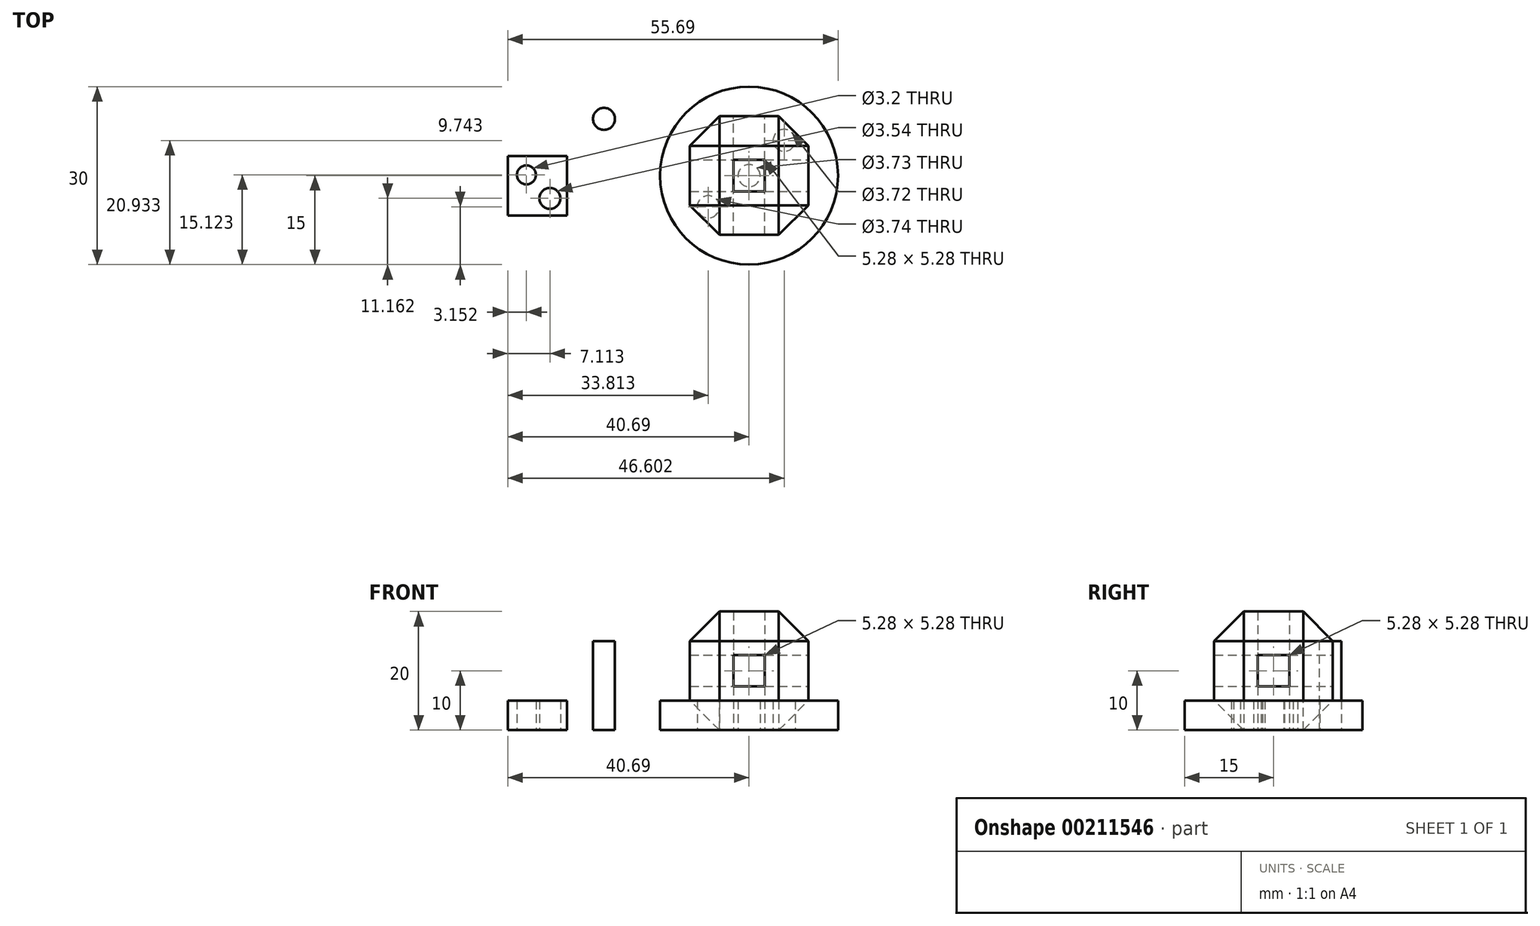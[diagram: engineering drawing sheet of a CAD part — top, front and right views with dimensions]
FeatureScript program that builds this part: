
annotation { "Feature Type Name" : "Feature", "Feature Type Description" : "" }
export const myFeature = defineFeature(function(context is Context, id is Id, definition is map)
    precondition{}
    {
        {
            var Q0;
            Q0=qCreatedBy(makeId("Top.planeOp"),FACE);
            var sketch = newSketch(context, id + "F0", { "sketchPlane" : qUnion([Q0])});
            skCircle(sketch, "E0", {"center": v(0, 0) * mm, "radius": 15 * mm});
            skCircle(sketch, "E1", {"center": v(0, 0) * mm, "radius": 1.87 * mm});
            skCircle(sketch, "E2", {"center": v(5.91, 5.93) * mm, "radius": 1.86 * mm});
            skCircle(sketch, "E3", {"center": v(-6.88, -5.26) * mm, "radius": 1.87 * mm});
            skSolve(sketch);
        }
        {
            var Q0;
            Q0=makeQuery(id+"F0.imprint","IMPRINT",FACE,{"disambiguationData":[TD([[makeQuery(id+"F0.imprint","IMPRINT",EDGE,{"derivedFrom":sQuery(id+"F0.wireOp",EDGE,"E0")}),1.0]])]});
            extrude(context, id + "F1", {"entities" : qUnion([Q0]), "depth" : 5 * mm});
        }
        {
            var Q0;
            Q0=qCreatedBy(makeId("Top.planeOp"),FACE);
            var sketch = newSketch(context, id + "F2", { "sketchPlane" : qUnion([Q0])});
            skCircle(sketch, "E4", {"center": v(-24.46, 9.56) * mm, "radius": 1.86 * mm});
            skSolve(sketch);
        }
        {
            var Q0;
            Q0=makeQuery(id+"F2.imprint","IMPRINT",FACE,{"disambiguationData":[TD([[makeQuery(id+"F2.imprint","IMPRINT",EDGE,{"derivedFrom":sQuery(id+"F2.wireOp",EDGE,"E4")}),1.0]])]});
            extrude(context, id + "F3", {"entities" : qUnion([Q0]), "depth" : 15 * mm});
        }
        {
            var Q0;
            Q0=qCreatedBy(makeId("Top.planeOp"),FACE);
            var sketch = newSketch(context, id + "F4", { "sketchPlane" : qUnion([Q0])});
            skLineSegment(sketch, "E5.bottom", {"start": v(-40.7, 3.28) * mm, "end": v(-30.7, 3.28) * mm});
            skLineSegment(sketch, "E5.top", {"start": v(-40.7, -6.72) * mm, "end": v(-30.7, -6.72) * mm});
            skLineSegment(sketch, "E5.left", {"start": v(-40.7, 3.28) * mm, "end": v(-40.7, -6.72) * mm});
            skLineSegment(sketch, "E5.right", {"start": v(-30.7, 3.28) * mm, "end": v(-30.7, -6.72) * mm});
            skCircle(sketch, "E6", {"center": v(-37.54, 0.12) * mm, "radius": 1.6 * mm});
            skCircle(sketch, "E7", {"center": v(-33.58, -3.84) * mm, "radius": 1.77 * mm});
            skLineSegment(sketch, "E8", {"start": v(-40.7, 3.28) * mm, "end": v(-30.7, -6.72) * mm, "construction": true});
            skSolve(sketch);
        }
        {
            var Q0;
            Q0 = qSketchRegion(id + "F4", true);
            extrude(context, id + "F5", {"entities" : qUnion([Q0]), "depth" : 5 * mm});
        }
        {
            var Q0;
            Q0=qCreatedBy(makeId("Top.planeOp"),FACE);
            var sketch = newSketch(context, id + "F6", { "sketchPlane" : qUnion([Q0])});
            skLineSegment(sketch, "E9.bottom", {"start": v(10, -10) * mm, "end": v(-10, -10) * mm});
            skLineSegment(sketch, "E9.top", {"start": v(10, 10) * mm, "end": v(-10, 10) * mm});
            skLineSegment(sketch, "E9.left", {"start": v(10, -10) * mm, "end": v(10, 10) * mm});
            skLineSegment(sketch, "E9.right", {"start": v(-10, -10) * mm, "end": v(-10, 10) * mm});
            skPoint(sketch, "E9.middle", {"position": v(0, 0) * mm});
            skLineSegment(sketch, "E10.bottom", {"start": v(2.64, -2.64) * mm, "end": v(-2.64, -2.64) * mm});
            skLineSegment(sketch, "E10.top", {"start": v(2.64, 2.64) * mm, "end": v(-2.64, 2.64) * mm});
            skLineSegment(sketch, "E10.left", {"start": v(2.64, -2.64) * mm, "end": v(2.64, 2.64) * mm});
            skLineSegment(sketch, "E10.right", {"start": v(-2.64, -2.64) * mm, "end": v(-2.64, 2.64) * mm});
            skSolve(sketch);
        }
        {
            var Q0;
            Q0 = qSketchRegion(id + "F6", true);
            extrude(context, id + "F7", {"entities" : qUnion([Q0]), "depth" : 20 * mm});
        }
        {
            var Q0;
            Q0=makeQuery(id+"F7.opExtrude","SWEPT_FACE",FACE,{"disambiguationData":[OSD([sQuery(id+"F6.wireOp",EDGE,"E9.top")])]});
            var sketch = newSketch(context, id + "F8", { "sketchPlane" : qUnion([Q0])});
            skLineSegment(sketch, "E11.0.0", {"start": v(-10, 0) * mm, "end": v(10, 0) * mm});
            skLineSegment(sketch, "E11.0.1", {"start": v(10, 0) * mm, "end": v(10, 20) * mm});
            skLineSegment(sketch, "E11.0.2", {"start": v(10, 20) * mm, "end": v(-10, 20) * mm});
            skLineSegment(sketch, "E11.0.3", {"start": v(-10, 20) * mm, "end": v(-10, 0) * mm});
            skLineSegment(sketch, "E12", {"start": v(-10, 10) * mm, "end": v(10, 10) * mm, "construction": true});
            skLineSegment(sketch, "E13", {"start": v(0, 0) * mm, "end": v(0, 20) * mm, "construction": true});
            skLineSegment(sketch, "E14.bottom", {"start": v(-2.64, 7.36) * mm, "end": v(2.64, 7.36) * mm});
            skLineSegment(sketch, "E14.top", {"start": v(-2.64, 12.64) * mm, "end": v(2.64, 12.64) * mm});
            skLineSegment(sketch, "E14.left", {"start": v(-2.64, 7.36) * mm, "end": v(-2.64, 12.64) * mm});
            skLineSegment(sketch, "E14.right", {"start": v(2.64, 7.36) * mm, "end": v(2.64, 12.64) * mm});
            skPoint(sketch, "E14.middle", {"position": v(0, 10) * mm});
            skSolve(sketch);
        }
        {
            var Q0;
            Q0=makeQuery(id+"F8.imprint","IMPRINT",FACE,{"disambiguationData":[TD([[makeQuery(id+"F8.imprint","IMPRINT",EDGE,{"derivedFrom":sQuery(id+"F8.wireOp",EDGE,"E14.bottom")}),1.0]])]});
            extrude(context, id + "F9", {"entities" : qUnion([Q0]), "operationType" : NewBodyOperationType.REMOVE, "oppositeDirection" : true, "depth" : 25 * mm});
        }
        {
            var Q0;
            Q0=makeQuery(id+"F7.opExtrude","SWEPT_FACE",FACE,{"disambiguationData":[OSD([sQuery(id+"F6.wireOp",EDGE,"E9.left")])]});
            var sketch = newSketch(context, id + "F10", { "sketchPlane" : qUnion([Q0])});
            skLineSegment(sketch, "E15", {"start": v(10, 10) * mm, "end": v(-10, 10) * mm, "construction": true});
            skLineSegment(sketch, "E16", {"start": v(0, 0) * mm, "end": v(0, 20) * mm, "construction": true});
            skLineSegment(sketch, "E17.bottom", {"start": v(2.64, 7.36) * mm, "end": v(-2.64, 7.36) * mm});
            skLineSegment(sketch, "E17.top", {"start": v(2.64, 12.64) * mm, "end": v(-2.64, 12.64) * mm});
            skLineSegment(sketch, "E17.left", {"start": v(2.64, 7.36) * mm, "end": v(2.64, 12.64) * mm});
            skLineSegment(sketch, "E17.right", {"start": v(-2.64, 7.36) * mm, "end": v(-2.64, 12.64) * mm});
            skPoint(sketch, "E17.middle", {"position": v(0, 10) * mm});
            skSolve(sketch);
        }
        {
            var Q0;
            Q0=makeQuery(id+"F10.imprint","IMPRINT",FACE,{"disambiguationData":[TD([[makeQuery(id+"F10.imprint","IMPRINT",EDGE,{"derivedFrom":sQuery(id+"F10.wireOp",EDGE,"E17.bottom")}),-1.0]])]});
            extrude(context, id + "F11", {"entities" : qUnion([Q0]), "operationType" : NewBodyOperationType.REMOVE, "oppositeDirection" : true, "depth" : 25 * mm});
        }
        {
            var Q0;
            Q0=makeQuery(id+"F7.opExtrude","CAP_EDGE",EDGE,{"disambiguationData":[OSD([sQuery(id+"F6.wireOp",EDGE,"E9.top")])],"isStart":true});
            var Q1;
            Q1=makeQuery(id+"F7.opExtrude","CAP_EDGE",EDGE,{"disambiguationData":[OSD([sQuery(id+"F6.wireOp",EDGE,"E9.top")])],"isStart":false});
            var Q2;
            Q2=makeQuery(id+"F7.opExtrude","CAP_EDGE",EDGE,{"disambiguationData":[OSD([sQuery(id+"F6.wireOp",EDGE,"E9.bottom")])],"isStart":false});
            var Q3;
            Q3=makeQuery(id+"F7.opExtrude","CAP_EDGE",EDGE,{"disambiguationData":[OSD([sQuery(id+"F6.wireOp",EDGE,"E9.bottom")])],"isStart":true});
            var Q4;
            Q4=makeQuery(id+"F7.opExtrude","CAP_EDGE",EDGE,{"disambiguationData":[OSD([sQuery(id+"F6.wireOp",EDGE,"E9.left")])],"isStart":true});
            var Q5;
            Q5=makeQuery(id+"F7.opExtrude","SWEPT_EDGE",EDGE,{"disambiguationData":[OSD([sQuery(id+"F6.wireOp",EDGE,"E9.top"),sQuery(id+"F6.wireOp",EDGE,"E9.left")])]});
            var Q6;
            Q6=makeQuery(id+"F7.opExtrude","CAP_EDGE",EDGE,{"disambiguationData":[OSD([sQuery(id+"F6.wireOp",EDGE,"E9.left")])],"isStart":false});
            var Q7;
            Q7=makeQuery(id+"F7.opExtrude","SWEPT_EDGE",EDGE,{"disambiguationData":[OSD([sQuery(id+"F6.wireOp",EDGE,"E9.bottom"),sQuery(id+"F6.wireOp",EDGE,"E9.left")])]});
            var Q8;
            Q8=makeQuery(id+"F7.opExtrude","SWEPT_EDGE",EDGE,{"disambiguationData":[OSD([sQuery(id+"F6.wireOp",EDGE,"E9.bottom"),sQuery(id+"F6.wireOp",EDGE,"E9.right")])]});
            var Q9;
            Q9=makeQuery(id+"F7.opExtrude","CAP_EDGE",EDGE,{"disambiguationData":[OSD([sQuery(id+"F6.wireOp",EDGE,"E9.right")])],"isStart":false});
            var Q10;
            Q10=makeQuery(id+"F7.opExtrude","SWEPT_EDGE",EDGE,{"disambiguationData":[OSD([sQuery(id+"F6.wireOp",EDGE,"E9.top"),sQuery(id+"F6.wireOp",EDGE,"E9.right")])]});
            var Q11;
            Q11=makeQuery(id+"F7.opExtrude","CAP_EDGE",EDGE,{"disambiguationData":[OSD([sQuery(id+"F6.wireOp",EDGE,"E9.right")])],"isStart":true});
            chamfer(context, id + "F12", {"entities" : qUnion([Q0, Q1, Q2, Q3, Q4, Q5, Q6, Q7, Q8, Q9, Q10, Q11]), "width" : 5 * mm, "tangentPropagation" : true});
        }
        {
            var Q0;
            Q0=makeQuery(id+"F6.imprint","IMPRINT",FACE,{"disambiguationData":[TD([[makeQuery(id+"F6.imprint","IMPRINT",EDGE,{"derivedFrom":sQuery(id+"F6.wireOp",EDGE,"E10.bottom")}),-1.0]])]});
            extrude(context, id + "F13", {"entities" : qUnion([Q0]), "depth" : 15 * mm});
        }
    });
